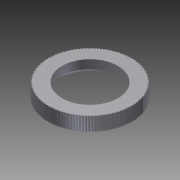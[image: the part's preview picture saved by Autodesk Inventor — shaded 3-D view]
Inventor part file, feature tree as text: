
AUTODESK INVENTOR PART (.ipt)
format: ipt  version: 2014 (Build 180170000, 170)  size: 379,392 bytes
history: native  units: in
note: dims shown in document units (in); Inventor stores cm internally (conversion verified against a paired STEP export)
features: other x7, sketch x2, extrude x1, hole x1
ambient origin geometry x8: Origin, YZ Plane, XZ Plane, XY Plane, X Axis, Y Axis, Z Axis, Center Point
bodies: Solid1 (feature_tree)
feature tree (11):
  extrude  "Extrusion1"  [1 undecoded]
  hole  "Drilling 1"  [1 undecoded]
  other  "1_XY"
  other  "1_YZ"
  other  "1_ZX"
  other  "1_X"
  other  "1_Y"
  other  "1_Z"
  other  "1_Center"
  sketch  "Sketch_1"  dims[d0=0.098in d1=0.0in]
  sketch  "Sketch2"  dims[d2=0.3979in d3=0.75in d4=0.4724in d5=0.25in d6=0.6184in d7=0.098in d8=0.0in]
note: 2 required parameter values undecoded (feature->parameter linkage not recoverable at this tier; creation-order binding heuristic only, values carry confidence <= 0.55)
